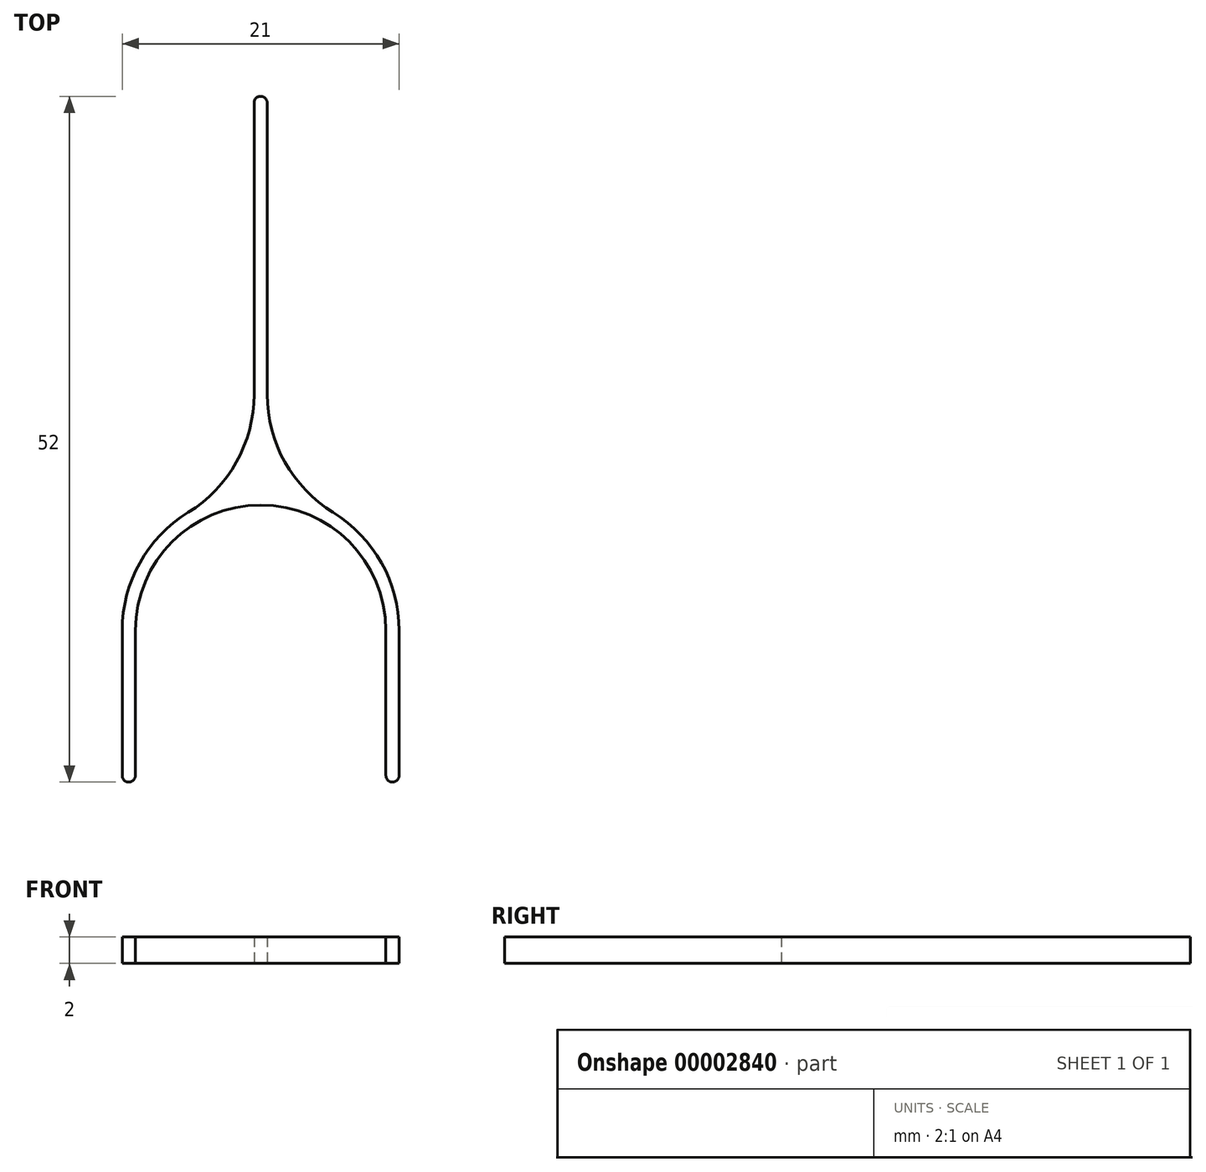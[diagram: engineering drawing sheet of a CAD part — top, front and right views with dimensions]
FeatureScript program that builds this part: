
annotation { "Feature Type Name" : "Feature", "Feature Type Description" : "" }
export const myFeature = defineFeature(function(context is Context, id is Id, definition is map)
    precondition{}
    {
        {
            var Q0;
            Q0=qCreatedBy(makeId("Top.planeOp"),FACE);
            var sketch = newSketch(context, id + "F0", { "sketchPlane" : qUnion([Q0])});
            skArc(sketch, "E0", {"start": v(9.5, 0) * mm, "mid": v(0, 9.5) * mm, "end": v(-9.5, 0) * mm});
            skArc(sketch, "E1", {"start": v(-10.5, -11) * mm, "mid": v(-10, -11.5) * mm, "end": v(-9.5, -11) * mm});
            skArc(sketch, "E2", {"start": v(9.5, -11) * mm, "mid": v(10, -11.5) * mm, "end": v(10.5, -11) * mm});
            skArc(sketch, "E3", {"start": v(0.5, 40) * mm, "mid": v(0, 40.5) * mm, "end": v(-0.5, 40) * mm});
            skArc(sketch, "E4", {"start": v(-5.5, 8.94) * mm, "mid": v(-9.17, 5.12) * mm, "end": v(-10.5, 0) * mm});
            skArc(sketch, "E5", {"start": v(10.5, 0) * mm, "mid": v(9.17, 5.12) * mm, "end": v(5.5, 8.94) * mm});
            skArc(sketch, "E6", {"start": v(0.5, 17.89) * mm, "mid": v(1.83, 12.77) * mm, "end": v(5.5, 8.94) * mm});
            skArc(sketch, "E7", {"start": v(-5.5, 8.94) * mm, "mid": v(-1.83, 12.77) * mm, "end": v(-0.5, 17.89) * mm});
            skLineSegment(sketch, "E8", {"start": v(-0.5, 40) * mm, "end": v(-0.5, 17.89) * mm});
            skLineSegment(sketch, "E9", {"start": v(0.5, 40) * mm, "end": v(0.5, 17.89) * mm});
            skLineSegment(sketch, "E10", {"start": v(-10.5, 0) * mm, "end": v(-10.5, -11) * mm});
            skLineSegment(sketch, "E11", {"start": v(-9.5, 0) * mm, "end": v(-9.5, -11) * mm});
            skLineSegment(sketch, "E12", {"start": v(9.5, 0) * mm, "end": v(9.5, -11) * mm});
            skLineSegment(sketch, "E13", {"start": v(10.5, 0) * mm, "end": v(10.5, -11) * mm});
            skSolve(sketch);
        }
        {
            var Q0;
            Q0=makeQuery(id+"F0.imprint","IMPRINT",FACE,{"disambiguationData":[TD([[makeQuery(id+"F0.imprint","IMPRINT",EDGE,{"derivedFrom":sQuery(id+"F0.wireOp",EDGE,"E0")}),-1.0]])]});
            extrude(context, id + "F1", {"entities" : qUnion([Q0]), "depth" : 2 * mm});
        }
    });
